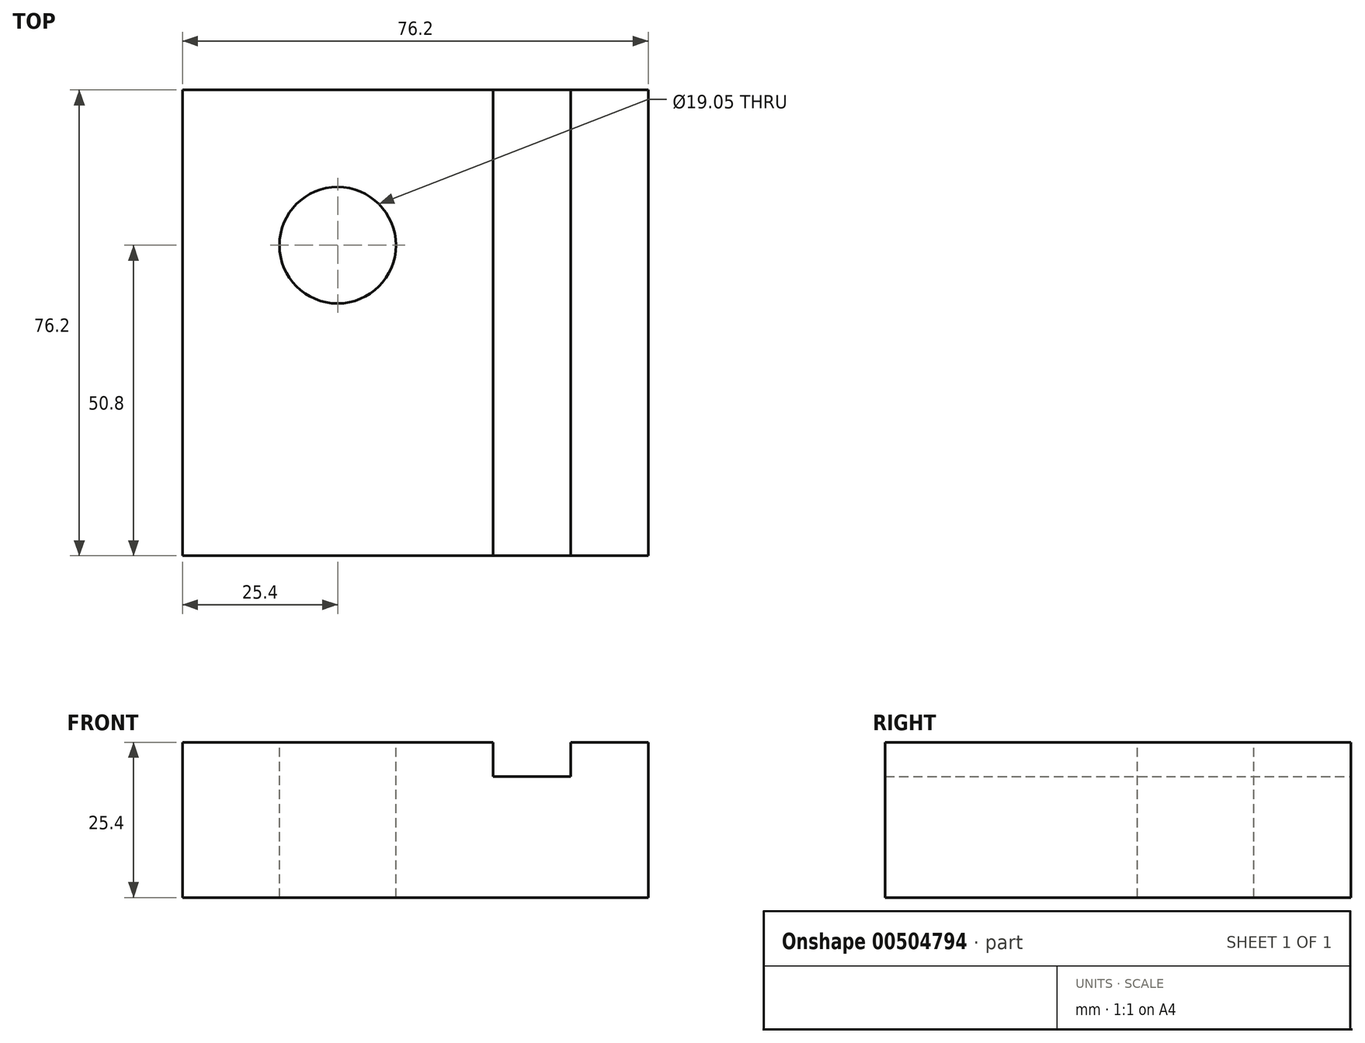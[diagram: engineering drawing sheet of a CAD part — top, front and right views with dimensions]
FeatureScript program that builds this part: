
annotation { "Feature Type Name" : "Feature", "Feature Type Description" : "" }
export const myFeature = defineFeature(function(context is Context, id is Id, definition is map)
    precondition{}
    {
        {
            var Q0;
            Q0=qCreatedBy(makeId("Front.planeOp"),FACE);
            var sketch = newSketch(context, id + "F0", { "sketchPlane" : qUnion([Q0])});
            skLineSegment(sketch, "E0.top", {"start": v(38.1, -12.7) * mm, "end": v(-38.1, -12.7) * mm});
            skLineSegment(sketch, "E0.left", {"start": v(38.1, 12.7) * mm, "end": v(38.1, -12.7) * mm});
            skLineSegment(sketch, "E0.right", {"start": v(-38.1, 12.7) * mm, "end": v(-38.1, -12.7) * mm});
            skPoint(sketch, "E0.middle", {"position": v(0, 0) * mm});
            skLineSegment(sketch, "E1", {"start": v(-38.1, 12.7) * mm, "end": v(12.7, 12.7) * mm});
            skLineSegment(sketch, "E2", {"start": v(12.7, 12.7) * mm, "end": v(12.7, 7.09) * mm});
            skLineSegment(sketch, "E3", {"start": v(12.7, 7.09) * mm, "end": v(25.4, 7.09) * mm});
            skLineSegment(sketch, "E4", {"start": v(25.4, 7.09) * mm, "end": v(25.4, 12.7) * mm});
            skLineSegment(sketch, "E5", {"start": v(25.4, 12.7) * mm, "end": v(38.1, 12.7) * mm});
            skSolve(sketch);
        }
        {
            var Q0;
            Q0=makeQuery(id+"F0.imprint","IMPRINT",FACE,{"disambiguationData":[TD([[makeQuery(id+"F0.imprint","IMPRINT",EDGE,{"derivedFrom":sQuery(id+"F0.wireOp",EDGE,"E0.top")}),-1.0]])]});
            extrude(context, id + "F1", {"entities" : qUnion([Q0]), "depth" : 76.2 * mm});
        }
        {
            var Q0;
            Q0=makeQuery(id+"F1.opExtrude","SWEPT_FACE",FACE,{"disambiguationData":[OSD([sQuery(id+"F0.wireOp",EDGE,"E1")])]});
            var sketch = newSketch(context, id + "F2", { "sketchPlane" : qUnion([Q0])});
            skLineSegment(sketch, "E6.bottom", {"start": v(-38.1, 0) * mm, "end": v(-12.7, 0) * mm});
            skLineSegment(sketch, "E6.top", {"start": v(-38.1, -25.4) * mm, "end": v(-12.7, -25.4) * mm});
            skLineSegment(sketch, "E6.left", {"start": v(-38.1, 0) * mm, "end": v(-38.1, -25.4) * mm});
            skLineSegment(sketch, "E6.right", {"start": v(-12.7, 0) * mm, "end": v(-12.7, -25.4) * mm});
            skCircle(sketch, "E7", {"center": v(-12.7, -25.4) * mm, "radius": 9.53 * mm});
            skSolve(sketch);
        }
        {
            var Q0;
            {var subQ0=sQuery(id+"F2.wireOp",EDGE,"E6.right");var subQ1=sQuery(id+"F2.wireOp",EDGE,"E6.top");var subQ2=makeQuery(id+"F2.imprint","INTERSECT",VERTEX,{"derivedFrom":[subQ1,subQ0]});Q0=makeQuery(id+"F2.imprint","IMPRINT",FACE,{"disambiguationData":[TD([[makeQuery(id+"F2.imprint","IMPRINT",EDGE,{"disambiguationData":[TD([[subQ2,1.0]])],"derivedFrom":subQ1}),-1.0]])]});}
            var Q1;
            {var subQ0=sQuery(id+"F2.wireOp",EDGE,"E6.right");var subQ1=sQuery(id+"F2.wireOp",EDGE,"E6.top");var subQ2=makeQuery(id+"F2.imprint","INTERSECT",VERTEX,{"derivedFrom":[subQ1,subQ0]});Q1=makeQuery(id+"F2.imprint","IMPRINT",FACE,{"disambiguationData":[TD([[makeQuery(id+"F2.imprint","IMPRINT",EDGE,{"disambiguationData":[TD([[subQ2,1.0]])],"derivedFrom":subQ1}),1.0]])]});}
            extrude(context, id + "F3", {"entities" : qUnion([Q0, Q1]), "operationType" : NewBodyOperationType.REMOVE, "oppositeDirection" : true, "depth" : 25.4 * mm});
        }
    });
